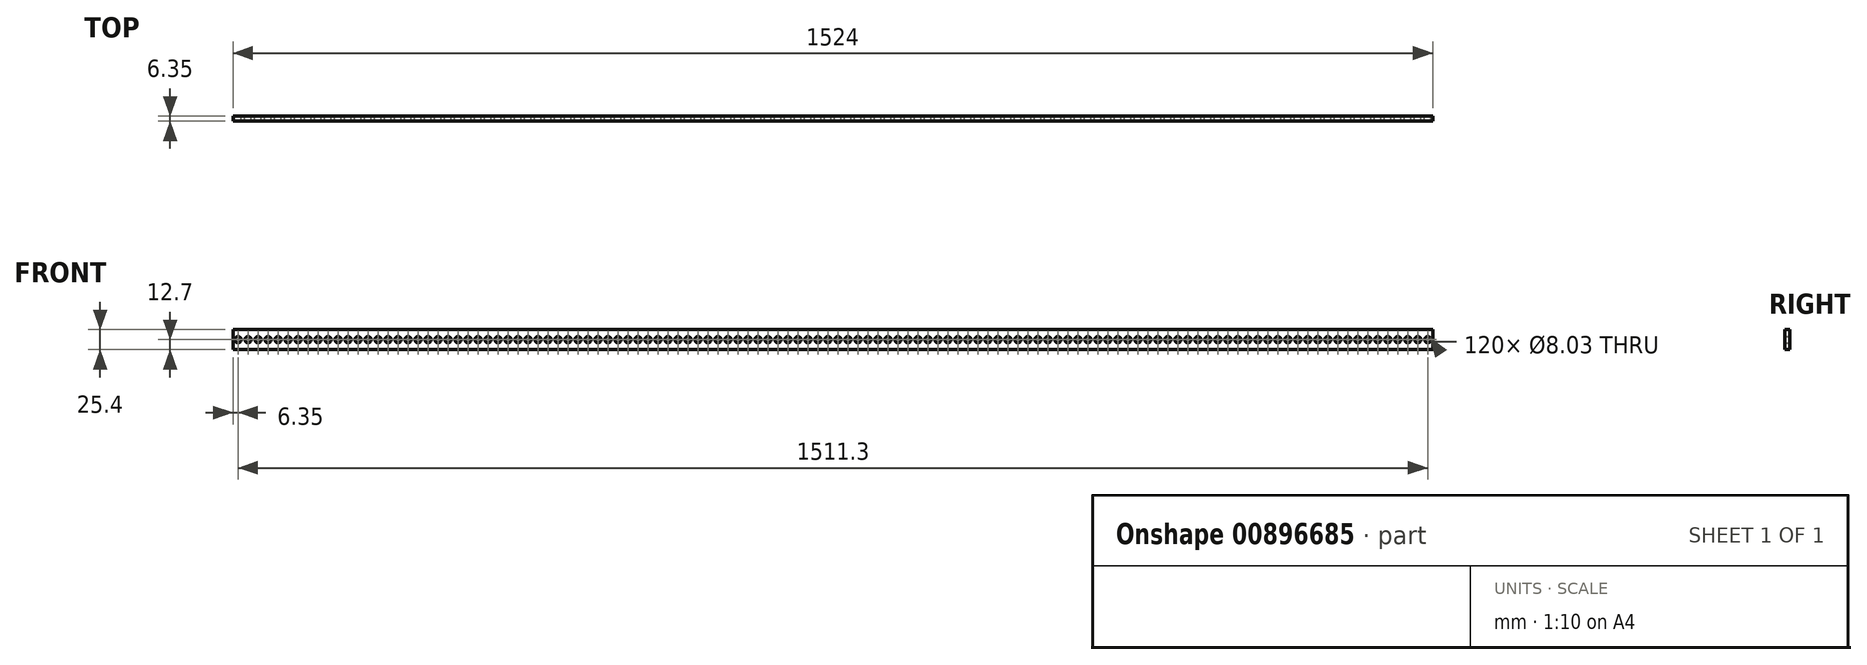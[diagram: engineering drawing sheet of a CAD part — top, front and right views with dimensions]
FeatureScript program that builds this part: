
annotation { "Feature Type Name" : "Feature", "Feature Type Description" : "" }
export const myFeature = defineFeature(function(context is Context, id is Id, definition is map)
    precondition{}
    {
        {
            var Q0;
            Q0=qCreatedBy(makeId("Front.planeOp"),FACE);
            var sketch = newSketch(context, id + "F0", { "sketchPlane" : qUnion([Q0])});
            skLineSegment(sketch, "E0.bottom", {"start": v(762, 12.7) * mm, "end": v(-762, 12.7) * mm});
            skLineSegment(sketch, "E0.top", {"start": v(762, -12.7) * mm, "end": v(-762, -12.7) * mm});
            skLineSegment(sketch, "E0.left", {"start": v(762, 12.7) * mm, "end": v(762, -12.7) * mm});
            skLineSegment(sketch, "E0.right", {"start": v(-762, 12.7) * mm, "end": v(-762, -12.7) * mm});
            skPoint(sketch, "E0.middle", {"position": v(0, 0) * mm});
            skCircle(sketch, "E1", {"center": v(-755.65, 0) * mm, "radius": 4.01 * mm});
            skCircle(sketch, "E2.1.0.0", {"center": v(-742.95, 0) * mm, "radius": 4.01 * mm});
            skCircle(sketch, "E2.2.0.0", {"center": v(-730.25, 0) * mm, "radius": 4.01 * mm});
            skCircle(sketch, "E2.3.0.0", {"center": v(-717.55, 0) * mm, "radius": 4.01 * mm});
            skCircle(sketch, "E2.4.0.0", {"center": v(-704.85, 0) * mm, "radius": 4.01 * mm});
            skCircle(sketch, "E2.5.0.0", {"center": v(-692.15, 0) * mm, "radius": 4.01 * mm});
            skCircle(sketch, "E2.6.0.0", {"center": v(-679.45, 0) * mm, "radius": 4.01 * mm});
            skCircle(sketch, "E2.7.0.0", {"center": v(-666.75, 0) * mm, "radius": 4.01 * mm});
            skCircle(sketch, "E2.8.0.0", {"center": v(-654.05, 0) * mm, "radius": 4.01 * mm});
            skCircle(sketch, "E2.9.0.0", {"center": v(-641.35, 0) * mm, "radius": 4.01 * mm});
            skCircle(sketch, "E2.10.0.0", {"center": v(-628.65, 0) * mm, "radius": 4.01 * mm});
            skCircle(sketch, "E2.11.0.0", {"center": v(-615.95, 0) * mm, "radius": 4.01 * mm});
            skCircle(sketch, "E2.12.0.0", {"center": v(-603.25, 0) * mm, "radius": 4.01 * mm});
            skCircle(sketch, "E2.13.0.0", {"center": v(-590.55, 0) * mm, "radius": 4.01 * mm});
            skCircle(sketch, "E2.14.0.0", {"center": v(-577.85, 0) * mm, "radius": 4.01 * mm});
            skCircle(sketch, "E2.15.0.0", {"center": v(-565.15, 0) * mm, "radius": 4.01 * mm});
            skCircle(sketch, "E2.16.0.0", {"center": v(-552.45, 0) * mm, "radius": 4.01 * mm});
            skCircle(sketch, "E2.17.0.0", {"center": v(-539.75, 0) * mm, "radius": 4.01 * mm});
            skCircle(sketch, "E2.18.0.0", {"center": v(-527.05, 0) * mm, "radius": 4.01 * mm});
            skCircle(sketch, "E2.19.0.0", {"center": v(-514.35, 0) * mm, "radius": 4.01 * mm});
            skCircle(sketch, "E2.20.0.0", {"center": v(-501.65, 0) * mm, "radius": 4.01 * mm});
            skCircle(sketch, "E2.21.0.0", {"center": v(-488.95, 0) * mm, "radius": 4.01 * mm});
            skCircle(sketch, "E2.22.0.0", {"center": v(-476.25, 0) * mm, "radius": 4.01 * mm});
            skCircle(sketch, "E2.23.0.0", {"center": v(-463.55, 0) * mm, "radius": 4.01 * mm});
            skCircle(sketch, "E2.24.0.0", {"center": v(-450.85, 0) * mm, "radius": 4.01 * mm});
            skCircle(sketch, "E2.25.0.0", {"center": v(-438.15, 0) * mm, "radius": 4.01 * mm});
            skCircle(sketch, "E2.26.0.0", {"center": v(-425.45, 0) * mm, "radius": 4.01 * mm});
            skCircle(sketch, "E2.27.0.0", {"center": v(-412.75, 0) * mm, "radius": 4.01 * mm});
            skCircle(sketch, "E2.28.0.0", {"center": v(-400.05, 0) * mm, "radius": 4.01 * mm});
            skCircle(sketch, "E2.29.0.0", {"center": v(-387.35, 0) * mm, "radius": 4.01 * mm});
            skCircle(sketch, "E2.30.0.0", {"center": v(-374.65, 0) * mm, "radius": 4.01 * mm});
            skCircle(sketch, "E2.31.0.0", {"center": v(-361.95, 0) * mm, "radius": 4.01 * mm});
            skCircle(sketch, "E2.32.0.0", {"center": v(-349.25, 0) * mm, "radius": 4.01 * mm});
            skCircle(sketch, "E2.33.0.0", {"center": v(-336.55, 0) * mm, "radius": 4.01 * mm});
            skCircle(sketch, "E2.34.0.0", {"center": v(-323.85, 0) * mm, "radius": 4.01 * mm});
            skCircle(sketch, "E2.35.0.0", {"center": v(-311.15, 0) * mm, "radius": 4.01 * mm});
            skCircle(sketch, "E2.36.0.0", {"center": v(-298.45, 0) * mm, "radius": 4.01 * mm});
            skCircle(sketch, "E2.37.0.0", {"center": v(-285.75, 0) * mm, "radius": 4.01 * mm});
            skCircle(sketch, "E2.38.0.0", {"center": v(-273.05, 0) * mm, "radius": 4.01 * mm});
            skCircle(sketch, "E2.39.0.0", {"center": v(-260.35, 0) * mm, "radius": 4.01 * mm});
            skCircle(sketch, "E2.40.0.0", {"center": v(-247.65, 0) * mm, "radius": 4.01 * mm});
            skCircle(sketch, "E2.41.0.0", {"center": v(-234.95, 0) * mm, "radius": 4.01 * mm});
            skCircle(sketch, "E2.42.0.0", {"center": v(-222.25, 0) * mm, "radius": 4.01 * mm});
            skCircle(sketch, "E2.43.0.0", {"center": v(-209.55, 0) * mm, "radius": 4.01 * mm});
            skCircle(sketch, "E2.44.0.0", {"center": v(-196.85, 0) * mm, "radius": 4.01 * mm});
            skCircle(sketch, "E2.45.0.0", {"center": v(-184.15, 0) * mm, "radius": 4.01 * mm});
            skCircle(sketch, "E2.46.0.0", {"center": v(-171.45, 0) * mm, "radius": 4.01 * mm});
            skCircle(sketch, "E2.47.0.0", {"center": v(-158.75, 0) * mm, "radius": 4.01 * mm});
            skCircle(sketch, "E2.48.0.0", {"center": v(-146.05, 0) * mm, "radius": 4.01 * mm});
            skCircle(sketch, "E2.49.0.0", {"center": v(-133.35, 0) * mm, "radius": 4.01 * mm});
            skCircle(sketch, "E2.50.0.0", {"center": v(-120.65, 0) * mm, "radius": 4.01 * mm});
            skCircle(sketch, "E2.51.0.0", {"center": v(-107.95, 0) * mm, "radius": 4.01 * mm});
            skCircle(sketch, "E2.52.0.0", {"center": v(-95.25, 0) * mm, "radius": 4.01 * mm});
            skCircle(sketch, "E2.53.0.0", {"center": v(-82.55, 0) * mm, "radius": 4.01 * mm});
            skCircle(sketch, "E2.54.0.0", {"center": v(-69.85, 0) * mm, "radius": 4.01 * mm});
            skCircle(sketch, "E2.55.0.0", {"center": v(-57.15, 0) * mm, "radius": 4.01 * mm});
            skCircle(sketch, "E2.56.0.0", {"center": v(-44.45, 0) * mm, "radius": 4.01 * mm});
            skCircle(sketch, "E2.57.0.0", {"center": v(-31.75, 0) * mm, "radius": 4.01 * mm});
            skCircle(sketch, "E2.58.0.0", {"center": v(-19.05, 0) * mm, "radius": 4.01 * mm});
            skCircle(sketch, "E2.59.0.0", {"center": v(-6.35, 0) * mm, "radius": 4.01 * mm});
            skCircle(sketch, "E2.60.0.0", {"center": v(6.35, 0) * mm, "radius": 4.01 * mm});
            skCircle(sketch, "E2.61.0.0", {"center": v(19.05, 0) * mm, "radius": 4.01 * mm});
            skCircle(sketch, "E2.62.0.0", {"center": v(31.75, 0) * mm, "radius": 4.01 * mm});
            skCircle(sketch, "E2.63.0.0", {"center": v(44.45, 0) * mm, "radius": 4.01 * mm});
            skCircle(sketch, "E2.64.0.0", {"center": v(57.15, 0) * mm, "radius": 4.01 * mm});
            skCircle(sketch, "E2.65.0.0", {"center": v(69.85, 0) * mm, "radius": 4.01 * mm});
            skCircle(sketch, "E2.66.0.0", {"center": v(82.55, 0) * mm, "radius": 4.01 * mm});
            skCircle(sketch, "E2.67.0.0", {"center": v(95.25, 0) * mm, "radius": 4.01 * mm});
            skCircle(sketch, "E2.68.0.0", {"center": v(107.95, 0) * mm, "radius": 4.01 * mm});
            skCircle(sketch, "E2.69.0.0", {"center": v(120.65, 0) * mm, "radius": 4.01 * mm});
            skCircle(sketch, "E2.70.0.0", {"center": v(133.35, 0) * mm, "radius": 4.01 * mm});
            skCircle(sketch, "E2.71.0.0", {"center": v(146.05, 0) * mm, "radius": 4.01 * mm});
            skCircle(sketch, "E2.72.0.0", {"center": v(158.75, 0) * mm, "radius": 4.01 * mm});
            skCircle(sketch, "E2.73.0.0", {"center": v(171.45, 0) * mm, "radius": 4.01 * mm});
            skCircle(sketch, "E2.74.0.0", {"center": v(184.15, 0) * mm, "radius": 4.01 * mm});
            skCircle(sketch, "E2.75.0.0", {"center": v(196.85, 0) * mm, "radius": 4.01 * mm});
            skCircle(sketch, "E2.76.0.0", {"center": v(209.55, 0) * mm, "radius": 4.01 * mm});
            skCircle(sketch, "E2.77.0.0", {"center": v(222.25, 0) * mm, "radius": 4.01 * mm});
            skCircle(sketch, "E2.78.0.0", {"center": v(234.95, 0) * mm, "radius": 4.01 * mm});
            skCircle(sketch, "E2.79.0.0", {"center": v(247.65, 0) * mm, "radius": 4.01 * mm});
            skCircle(sketch, "E2.80.0.0", {"center": v(260.35, 0) * mm, "radius": 4.01 * mm});
            skCircle(sketch, "E2.81.0.0", {"center": v(273.05, 0) * mm, "radius": 4.01 * mm});
            skCircle(sketch, "E2.82.0.0", {"center": v(285.75, 0) * mm, "radius": 4.01 * mm});
            skCircle(sketch, "E2.83.0.0", {"center": v(298.45, 0) * mm, "radius": 4.01 * mm});
            skCircle(sketch, "E2.84.0.0", {"center": v(311.15, 0) * mm, "radius": 4.01 * mm});
            skCircle(sketch, "E2.85.0.0", {"center": v(323.85, 0) * mm, "radius": 4.01 * mm});
            skCircle(sketch, "E2.86.0.0", {"center": v(336.55, 0) * mm, "radius": 4.01 * mm});
            skCircle(sketch, "E2.87.0.0", {"center": v(349.25, 0) * mm, "radius": 4.01 * mm});
            skCircle(sketch, "E2.88.0.0", {"center": v(361.95, 0) * mm, "radius": 4.01 * mm});
            skCircle(sketch, "E2.89.0.0", {"center": v(374.65, 0) * mm, "radius": 4.01 * mm});
            skCircle(sketch, "E2.90.0.0", {"center": v(387.35, 0) * mm, "radius": 4.01 * mm});
            skCircle(sketch, "E2.91.0.0", {"center": v(400.05, 0) * mm, "radius": 4.01 * mm});
            skCircle(sketch, "E2.92.0.0", {"center": v(412.75, 0) * mm, "radius": 4.01 * mm});
            skCircle(sketch, "E2.93.0.0", {"center": v(425.45, 0) * mm, "radius": 4.01 * mm});
            skCircle(sketch, "E2.94.0.0", {"center": v(438.15, 0) * mm, "radius": 4.01 * mm});
            skCircle(sketch, "E2.95.0.0", {"center": v(450.85, 0) * mm, "radius": 4.01 * mm});
            skCircle(sketch, "E2.96.0.0", {"center": v(463.55, 0) * mm, "radius": 4.01 * mm});
            skCircle(sketch, "E2.97.0.0", {"center": v(476.25, 0) * mm, "radius": 4.01 * mm});
            skCircle(sketch, "E2.98.0.0", {"center": v(488.95, 0) * mm, "radius": 4.01 * mm});
            skLineSegment(sketch, "E2.direction1", {"start": v(-755.65, 0) * mm, "end": v(-742.95, 0) * mm, "construction": true});
            skCircle(sketch, "E3.1.0.0", {"center": v(501.65, 0) * mm, "radius": 4.01 * mm});
            skCircle(sketch, "E3.2.0.0", {"center": v(514.35, 0) * mm, "radius": 4.01 * mm});
            skCircle(sketch, "E3.3.0.0", {"center": v(527.05, 0) * mm, "radius": 4.01 * mm});
            skCircle(sketch, "E3.4.0.0", {"center": v(539.75, 0) * mm, "radius": 4.01 * mm});
            skCircle(sketch, "E3.5.0.0", {"center": v(552.45, 0) * mm, "radius": 4.01 * mm});
            skCircle(sketch, "E3.6.0.0", {"center": v(565.15, 0) * mm, "radius": 4.01 * mm});
            skCircle(sketch, "E3.7.0.0", {"center": v(577.85, 0) * mm, "radius": 4.01 * mm});
            skCircle(sketch, "E3.8.0.0", {"center": v(590.55, 0) * mm, "radius": 4.01 * mm});
            skCircle(sketch, "E3.9.0.0", {"center": v(603.25, 0) * mm, "radius": 4.01 * mm});
            skCircle(sketch, "E3.10.0.0", {"center": v(615.95, 0) * mm, "radius": 4.01 * mm});
            skCircle(sketch, "E3.11.0.0", {"center": v(628.65, 0) * mm, "radius": 4.01 * mm});
            skCircle(sketch, "E3.12.0.0", {"center": v(641.35, 0) * mm, "radius": 4.01 * mm});
            skCircle(sketch, "E3.13.0.0", {"center": v(654.05, 0) * mm, "radius": 4.01 * mm});
            skCircle(sketch, "E3.14.0.0", {"center": v(666.75, 0) * mm, "radius": 4.01 * mm});
            skCircle(sketch, "E3.15.0.0", {"center": v(679.45, 0) * mm, "radius": 4.01 * mm});
            skCircle(sketch, "E3.16.0.0", {"center": v(692.15, 0) * mm, "radius": 4.01 * mm});
            skCircle(sketch, "E3.17.0.0", {"center": v(704.85, 0) * mm, "radius": 4.01 * mm});
            skCircle(sketch, "E3.18.0.0", {"center": v(717.55, 0) * mm, "radius": 4.01 * mm});
            skCircle(sketch, "E3.19.0.0", {"center": v(730.25, 0) * mm, "radius": 4.01 * mm});
            skCircle(sketch, "E3.20.0.0", {"center": v(742.95, 0) * mm, "radius": 4.01 * mm});
            skLineSegment(sketch, "E3.direction1", {"start": v(488.95, 0) * mm, "end": v(501.65, 0) * mm, "construction": true});
            skCircle(sketch, "E4.0.21.0", {"center": v(755.65, 0) * mm, "radius": 4.01 * mm});
            skSolve(sketch);
        }
        {
            var Q0;
            Q0=makeQuery(id+"F0.imprint","IMPRINT",FACE,{"disambiguationData":[TD([[makeQuery(id+"F0.imprint","IMPRINT",EDGE,{"derivedFrom":sQuery(id+"F0.wireOp",EDGE,"E0.bottom")}),1.0]])]});
            extrude(context, id + "F1", {"entities" : qUnion([Q0]), "depth" : 6.35 * mm, "offsetDistance" : 25.4 * mm});
        }
    });
